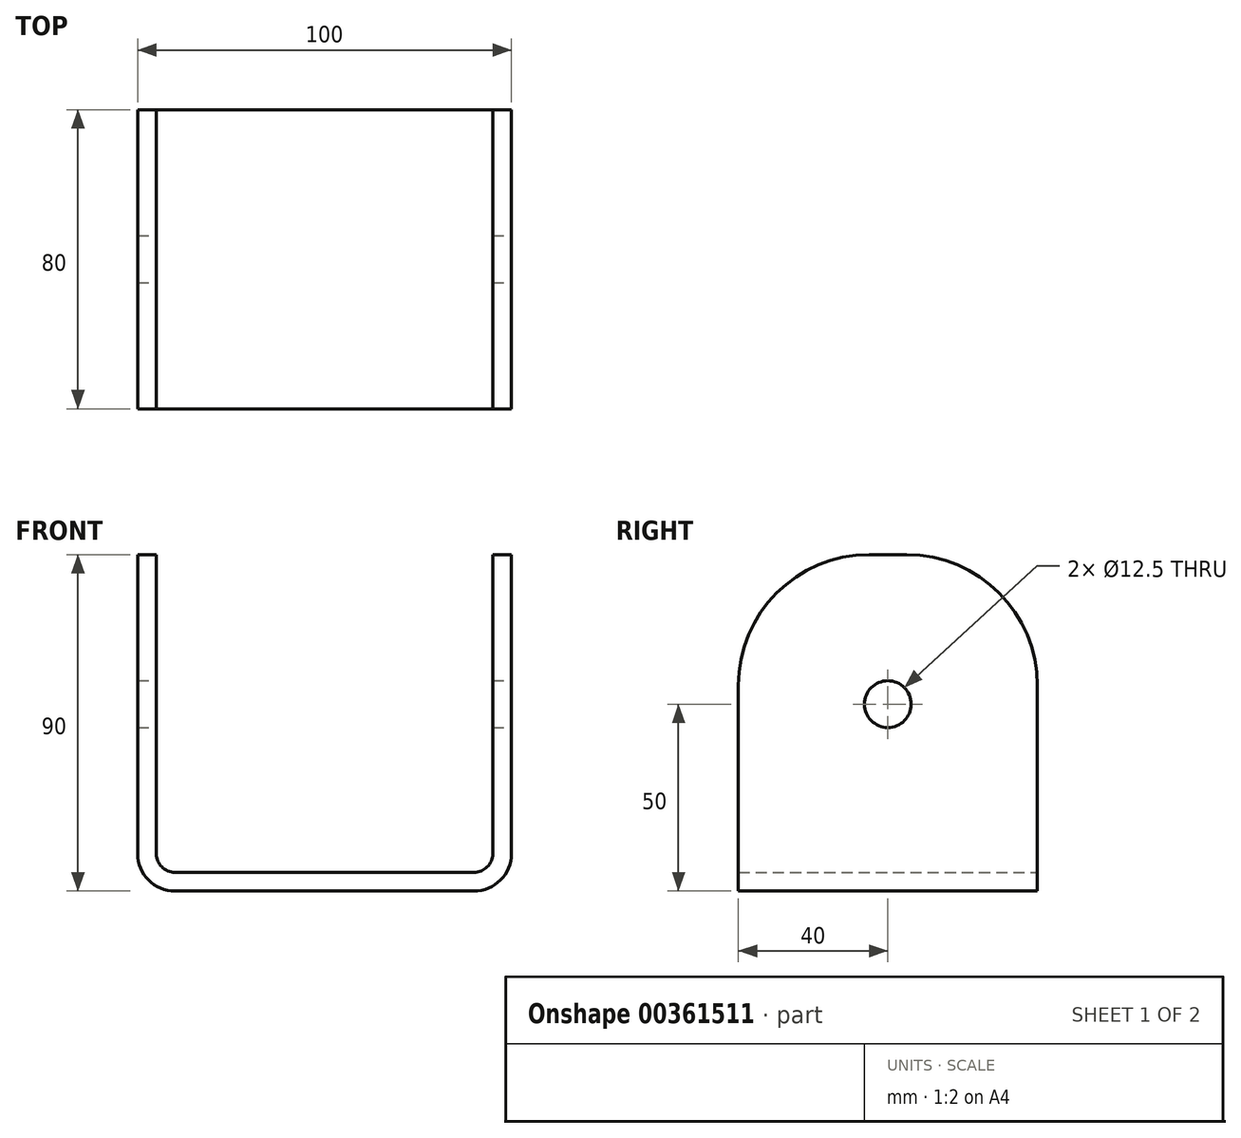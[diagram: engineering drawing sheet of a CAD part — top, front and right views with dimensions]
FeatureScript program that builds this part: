
annotation { "Feature Type Name" : "Feature", "Feature Type Description" : "" }
export const myFeature = defineFeature(function(context is Context, id is Id, definition is map)
    precondition{}
    {
        {
            var Q0;
            Q0=qCreatedBy(makeId("Front.planeOp"),FACE);
            var sketch = newSketch(context, id + "F0", { "sketchPlane" : qUnion([Q0])});
            skLineSegment(sketch, "E0.bottom", {"start": v(40, 50) * mm, "end": v(-40, 50) * mm});
            skLineSegment(sketch, "E0.top", {"start": v(40, -50) * mm, "end": v(-40, -50) * mm});
            skLineSegment(sketch, "E0.left", {"start": v(50, 40) * mm, "end": v(50, -40) * mm});
            skLineSegment(sketch, "E0.right", {"start": v(-50, 40) * mm, "end": v(-50, -40) * mm});
            skPoint(sketch, "E0.middle", {"position": v(0, 0) * mm});
            skPoint(sketch, "E1.visualSharp", {"position": v(-50, 50) * mm});
            skArc(sketch, "E1.filletArc", {"start": v(-40, 50) * mm, "mid": v(-47.07, 47.07) * mm, "end": v(-50, 40) * mm});
            skPoint(sketch, "E2.visualSharp", {"position": v(50, 50) * mm});
            skArc(sketch, "E2.filletArc", {"start": v(50, 40) * mm, "mid": v(47.07, 47.07) * mm, "end": v(40, 50) * mm});
            skPoint(sketch, "E3.visualSharp", {"position": v(50, -50) * mm});
            skArc(sketch, "E3.filletArc", {"start": v(40, -50) * mm, "mid": v(47.07, -47.07) * mm, "end": v(50, -40) * mm});
            skPoint(sketch, "E4.visualSharp", {"position": v(-50, -50) * mm});
            skArc(sketch, "E4.filletArc", {"start": v(-50, -40) * mm, "mid": v(-47.07, -47.07) * mm, "end": v(-40, -50) * mm});
            skArc(sketch, "E5.0", {"start": v(45, 40) * mm, "mid": v(43.54, 43.54) * mm, "end": v(40, 45) * mm});
            skLineSegment(sketch, "E5.1", {"start": v(45, 40) * mm, "end": v(45, -40) * mm});
            skLineSegment(sketch, "E5.2", {"start": v(40, 45) * mm, "end": v(-40, 45) * mm});
            skArc(sketch, "E5.3", {"start": v(40, -45) * mm, "mid": v(43.54, -43.54) * mm, "end": v(45, -40) * mm});
            skArc(sketch, "E5.4", {"start": v(-40, 45) * mm, "mid": v(-43.54, 43.54) * mm, "end": v(-45, 40) * mm});
            skLineSegment(sketch, "E5.5", {"start": v(-45, 40) * mm, "end": v(-45, -40) * mm});
            skArc(sketch, "E5.6", {"start": v(-45, -40) * mm, "mid": v(-43.54, -43.54) * mm, "end": v(-40, -45) * mm});
            skLineSegment(sketch, "E5.7", {"start": v(40, -45) * mm, "end": v(-40, -45) * mm});
            skSolve(sketch);
        }
        {
            var Q0;
            Q0=qSketchRegion(id+"F0",true);
            extrude(context, id + "F1", {"entities" : qUnion([Q0]), "endBound" : BoundingType.SYMMETRIC, "depth" : 80 * mm});
        }
        {
            var Q0;
            Q0=makeQuery(id+"F1.opExtrude","SWEPT_FACE",FACE,{"disambiguationData":[OSD([sQuery(id+"F0.wireOp",EDGE,"E0.left")])]});
            var sketch = newSketch(context, id + "F2", { "sketchPlane" : qUnion([Q0])});
            skLineSegment(sketch, "E6", {"start": v(-40, -40) * mm, "end": v(-40, 5) * mm, "construction": true});
            skLineSegment(sketch, "E7", {"start": v(-5, 40) * mm, "end": v(5, 40) * mm});
            skLineSegment(sketch, "E8", {"start": v(40, 5) * mm, "end": v(40, -40) * mm, "construction": true});
            skPoint(sketch, "E9.visualSharp", {"position": v(-40, 40) * mm});
            skArc(sketch, "E9.filletArc", {"start": v(-5, 40) * mm, "mid": v(-29.75, 29.75) * mm, "end": v(-40, 5) * mm});
            skPoint(sketch, "E10.visualSharp", {"position": v(40, 40) * mm});
            skArc(sketch, "E10.filletArc", {"start": v(40, 5) * mm, "mid": v(29.75, 29.75) * mm, "end": v(5, 40) * mm});
            skCircle(sketch, "E11", {"center": v(0, 0) * mm, "radius": 6.25 * mm});
            skLineSegment(sketch, "E12", {"start": v(-40, 5) * mm, "end": v(-40, 50) * mm});
            skLineSegment(sketch, "E13", {"start": v(-40, 50) * mm, "end": v(40, 50) * mm});
            skLineSegment(sketch, "E14", {"start": v(40, 50) * mm, "end": v(40, 5) * mm});
            skSolve(sketch);
        }
        {
            var Q0;
            Q0 = qSketchRegion(id + "F2", true);
            extrude(context, id + "F3", {"entities" : qUnion([Q0]), "operationType" : NewBodyOperationType.REMOVE, "endBound" : BoundingType.THROUGH_ALL, "oppositeDirection" : true, "depth" : 25 * mm});
        }
    });
